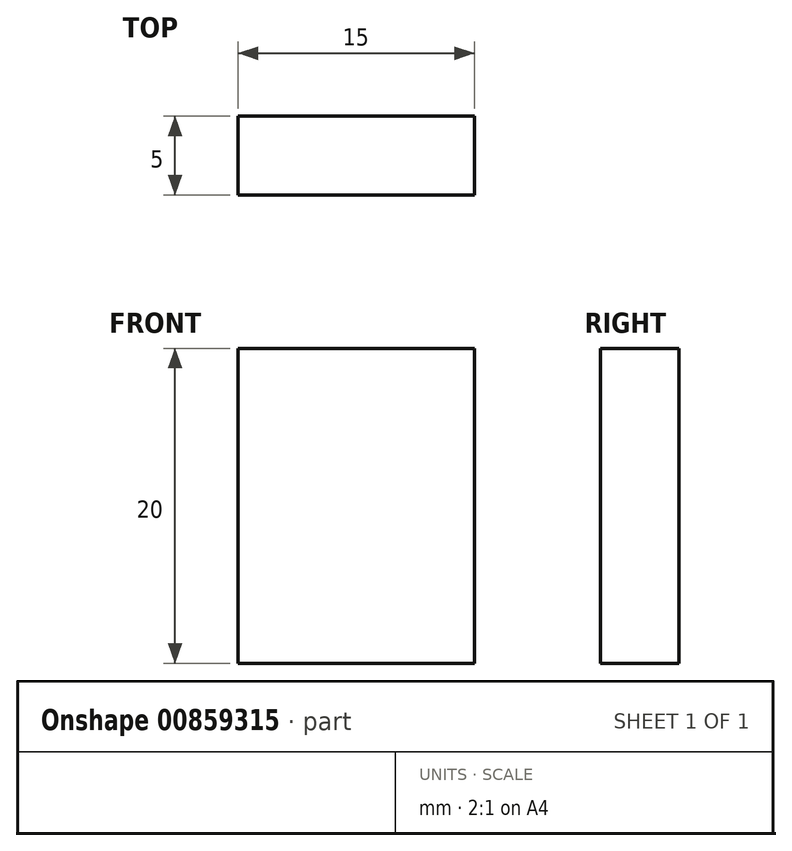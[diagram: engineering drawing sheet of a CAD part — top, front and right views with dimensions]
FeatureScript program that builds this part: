
annotation { "Feature Type Name" : "Feature", "Feature Type Description" : "" }
export const myFeature = defineFeature(function(context is Context, id is Id, definition is map)
    precondition{}
    {
        {
            var Q0;
            Q0=qCreatedBy(makeId("Front.planeOp"),FACE);
            var sketch = newSketch(context, id + "F0", { "sketchPlane" : qUnion([Q0])});
            skLineSegment(sketch, "E0.bottom", {"start": v(-7.5, 14.44) * mm, "end": v(7.5, 14.44) * mm});
            skLineSegment(sketch, "E0.top", {"start": v(-7.5, -5.56) * mm, "end": v(7.5, -5.56) * mm});
            skLineSegment(sketch, "E0.left", {"start": v(-7.5, 14.44) * mm, "end": v(-7.5, -5.56) * mm});
            skLineSegment(sketch, "E0.right", {"start": v(7.5, 14.44) * mm, "end": v(7.5, -5.56) * mm});
            skPoint(sketch, "E0.middle", {"position": v(0, 4.44) * mm});
            skSolve(sketch);
        }
        {
            var Q0;
            Q0=makeQuery(id+"F0.imprint","IMPRINT",FACE,{"disambiguationData":[TD([[makeQuery(id+"F0.imprint","IMPRINT",EDGE,{"derivedFrom":sQuery(id+"F0.wireOp",EDGE,"E0.bottom")}),-1.0]])]});
            extrude(context, id + "F1", {"entities" : qUnion([Q0]), "depth" : 5 * mm, "offsetDistance" : 25.4 * mm});
        }
    });
